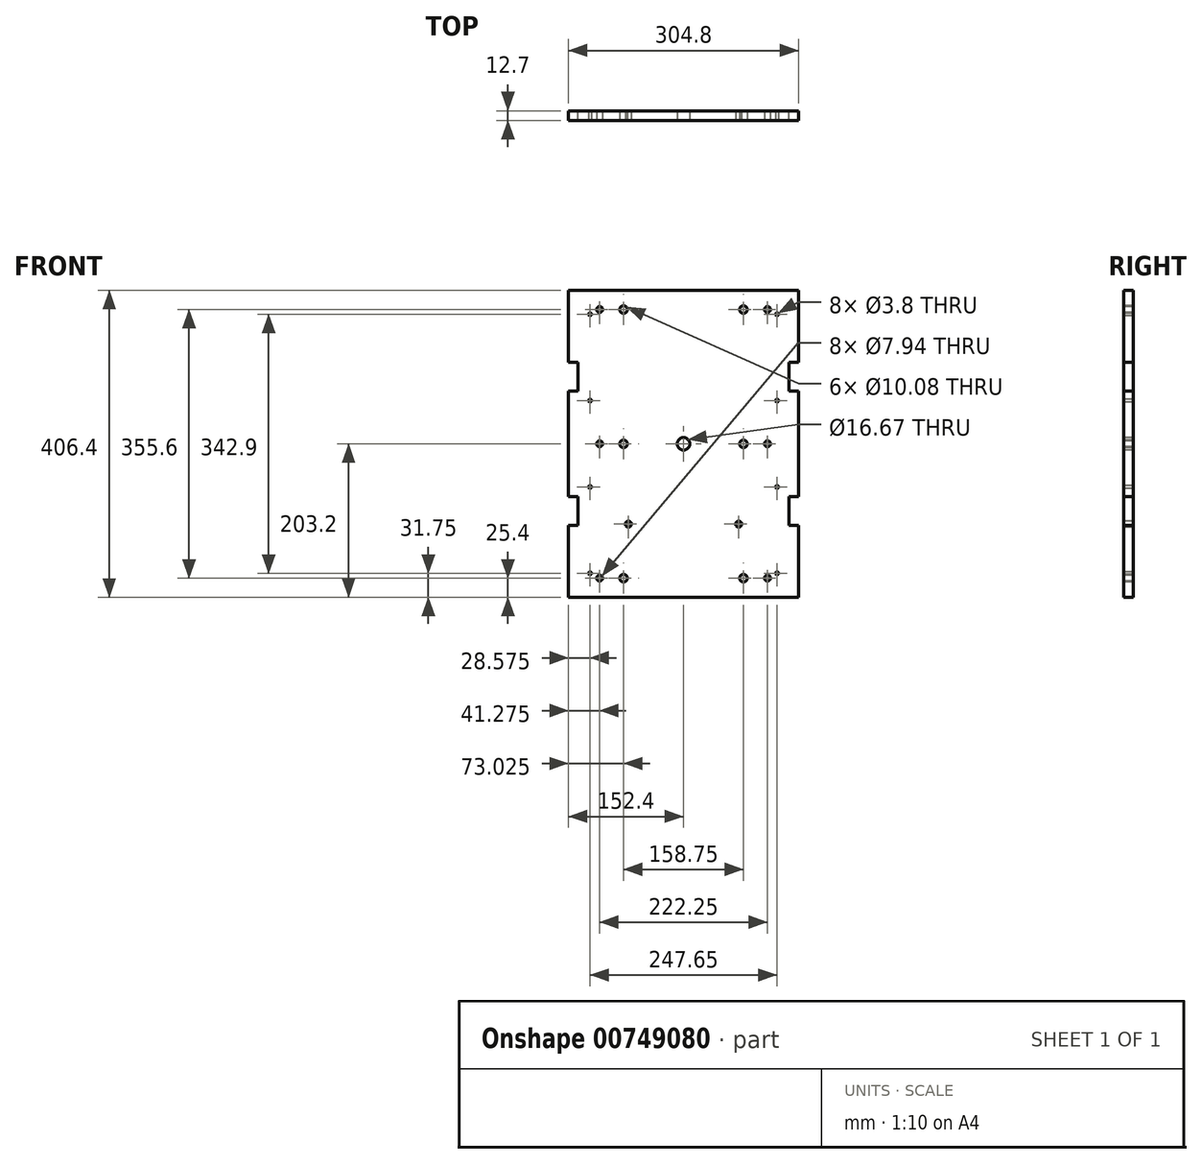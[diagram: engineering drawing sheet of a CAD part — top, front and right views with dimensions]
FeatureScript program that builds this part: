
annotation { "Feature Type Name" : "Feature", "Feature Type Description" : "" }
export const myFeature = defineFeature(function(context is Context, id is Id, definition is map)
    precondition{}
    {
        {
            var Q0;
            Q0=qCreatedBy(makeId("Front.planeOp"),FACE);
            var sketch = newSketch(context, id + "F0", { "sketchPlane" : qUnion([Q0])});
            skLineSegment(sketch, "E0.bottom", {"start": v(0, 0) * mm, "end": v(-304.8, 0) * mm});
            skLineSegment(sketch, "E0.top", {"start": v(0, 406.4) * mm, "end": v(-304.8, 406.4) * mm});
            skLineSegment(sketch, "E0.left", {"start": v(0, 0) * mm, "end": v(0, 95.22) * mm});
            skLineSegment(sketch, "E0.right", {"start": v(-304.8, 0) * mm, "end": v(-304.8, 95.22) * mm});
            skLineSegment(sketch, "E1", {"start": v(-152.4, 0) * mm, "end": v(-152.4, 406.4) * mm, "construction": true});
            skLineSegment(sketch, "E2", {"start": v(-304.8, 203.2) * mm, "end": v(0, 203.2) * mm, "construction": true});
            skPoint(sketch, "E3", {"position": v(-41.28, 381) * mm});
            skPoint(sketch, "E4", {"position": v(-73.03, 381) * mm});
            skLineSegment(sketch, "E5", {"start": v(-73.03, 381) * mm, "end": v(-73.03, 203.2) * mm, "construction": true});
            skLineSegment(sketch, "E6", {"start": v(-41.28, 381) * mm, "end": v(-41.28, 203.2) * mm, "construction": true});
            skPoint(sketch, "E7", {"position": v(-73.03, 203.2) * mm});
            skPoint(sketch, "E8", {"position": v(-41.28, 203.2) * mm});
            skPoint(sketch, "E9", {"position": v(-152.4, 203.2) * mm});
            skLineSegment(sketch, "E10", {"start": v(-28.58, 406.4) * mm, "end": v(-28.58, 203.2) * mm, "construction": true});
            skPoint(sketch, "E11", {"position": v(-28.58, 374.65) * mm});
            skPoint(sketch, "E12", {"position": v(-28.58, 260.35) * mm});
            skPoint(sketch, "E13.MirrorP", {"position": v(-28.58, 146.05) * mm});
            skPoint(sketch, "E14.MirrorP", {"position": v(-28.57, 31.75) * mm});
            skPoint(sketch, "E15.MirrorP", {"position": v(-41.27, 25.4) * mm});
            skPoint(sketch, "E16.MirrorP", {"position": v(-73.02, 25.4) * mm});
            skPoint(sketch, "E17.MirrorP", {"position": v(-276.22, 146.05) * mm});
            skPoint(sketch, "E18.MirrorP", {"position": v(-231.78, 25.4) * mm});
            skPoint(sketch, "E19.MirrorP", {"position": v(-263.53, 25.4) * mm});
            skPoint(sketch, "E20.MirrorP", {"position": v(-276.23, 31.75) * mm});
            skPoint(sketch, "E21.MirrorP", {"position": v(-276.22, 260.35) * mm});
            skPoint(sketch, "E22.MirrorP", {"position": v(-276.23, 374.65) * mm});
            skPoint(sketch, "E23.MirrorP", {"position": v(-263.53, 381) * mm});
            skPoint(sketch, "E24.MirrorP", {"position": v(-231.78, 381) * mm});
            skLineSegment(sketch, "E25", {"start": v(-304.8, 292.1) * mm, "end": v(-152.4, 292.1) * mm, "construction": true});
            skLineSegment(sketch, "E26", {"start": v(-304.8, 311.18) * mm, "end": v(-292.07, 311.18) * mm});
            skLineSegment(sketch, "E27", {"start": v(-292.07, 311.18) * mm, "end": v(-292.07, 273.02) * mm});
            skLineSegment(sketch, "E28", {"start": v(-292.07, 273.02) * mm, "end": v(-304.8, 273.02) * mm});
            skLineSegment(sketch, "E29.trimOffspring", {"start": v(-304.8, 311.18) * mm, "end": v(-304.8, 406.4) * mm});
            skLineSegment(sketch, "E30.MirrorCS", {"start": v(-304.8, 95.22) * mm, "end": v(-292.07, 95.22) * mm});
            skLineSegment(sketch, "E31.MirrorCS", {"start": v(-292.07, 95.22) * mm, "end": v(-292.07, 133.38) * mm});
            skLineSegment(sketch, "E32.MirrorCS", {"start": v(-292.07, 133.38) * mm, "end": v(-304.8, 133.38) * mm});
            skLineSegment(sketch, "E33.MirrorCS", {"start": v(-12.73, 95.22) * mm, "end": v(-12.73, 133.38) * mm});
            skLineSegment(sketch, "E34.MirrorCS", {"start": v(-12.73, 133.38) * mm, "end": v(0, 133.38) * mm});
            skLineSegment(sketch, "E35.MirrorCS", {"start": v(0, 95.22) * mm, "end": v(-12.73, 95.22) * mm});
            skLineSegment(sketch, "E36.MirrorCS", {"start": v(-12.73, 273.02) * mm, "end": v(0, 273.02) * mm});
            skLineSegment(sketch, "E37.MirrorCS", {"start": v(-12.73, 311.18) * mm, "end": v(-12.73, 273.02) * mm});
            skLineSegment(sketch, "E38.MirrorCS", {"start": v(0, 311.18) * mm, "end": v(-12.73, 311.18) * mm});
            skLineSegment(sketch, "E39.trimOffspring", {"start": v(-304.8, 133.38) * mm, "end": v(-304.8, 273.02) * mm});
            skLineSegment(sketch, "E40.trimOffspring", {"start": v(0, 133.38) * mm, "end": v(0, 273.02) * mm});
            skLineSegment(sketch, "E41.trimOffspring", {"start": v(0, 311.18) * mm, "end": v(0, 406.4) * mm});
            skPoint(sketch, "E42.MirrorP", {"position": v(-231.78, 203.2) * mm});
            skPoint(sketch, "E43.MirrorP", {"position": v(-263.53, 203.2) * mm});
            skLineSegment(sketch, "E44", {"start": v(-152.4, 96.84) * mm, "end": v(-304.8, 96.84) * mm, "construction": true});
            skPoint(sketch, "E45", {"position": v(-225.42, 96.84) * mm});
            skPoint(sketch, "E46.MirrorP", {"position": v(-79.38, 96.84) * mm});
            skSolve(sketch);
        }
        {
            var Q0;
            Q0 = qSketchRegion(id + "F0", true);
            extrude(context, id + "F1", {"entities" : qUnion([Q0]), "depth" : 12.7 * mm, "offsetDistance" : 25.4 * mm});
        }
        {
            var Q0;
            Q0=sQuery(id+"F0.wireOp",VERTEX,"E22.MirrorP");
            var Q1;
            Q1=sQuery(id+"F0.wireOp",VERTEX,"E21.MirrorP");
            var Q2;
            Q2=sQuery(id+"F0.wireOp",VERTEX,"E17.MirrorP");
            var Q3;
            Q3=sQuery(id+"F0.wireOp",VERTEX,"E20.MirrorP");
            var Q4;
            Q4=sQuery(id+"F0.wireOp",VERTEX,"E11");
            var Q5;
            Q5=sQuery(id+"F0.wireOp",VERTEX,"E12");
            var Q6;
            Q6=sQuery(id+"F0.wireOp",VERTEX,"E13.MirrorP");
            var Q7;
            Q7=sQuery(id+"F0.wireOp",VERTEX,"E14.MirrorP");
            var Q8;
            Q8=makeQuery(id+"F1.opExtrude","SWEPT_BODY",BODY,{"disambiguationData":[OSD([sQuery(id+"F0.wireOp",EDGE,"E0.bottom"),sQuery(id+"F0.wireOp",EDGE,"E0.top"),sQuery(id+"F0.wireOp",EDGE,"E0.left"),sQuery(id+"F0.wireOp",EDGE,"E0.right"),sQuery(id+"F0.wireOp",EDGE,"E26"),sQuery(id+"F0.wireOp",EDGE,"E27"),sQuery(id+"F0.wireOp",EDGE,"E28"),sQuery(id+"F0.wireOp",EDGE,"E29.trimOffspring"),sQuery(id+"F0.wireOp",EDGE,"E30.MirrorCS"),sQuery(id+"F0.wireOp",EDGE,"E31.MirrorCS"),sQuery(id+"F0.wireOp",EDGE,"E32.MirrorCS"),sQuery(id+"F0.wireOp",EDGE,"E33.MirrorCS"),sQuery(id+"F0.wireOp",EDGE,"E34.MirrorCS"),sQuery(id+"F0.wireOp",EDGE,"E35.MirrorCS"),sQuery(id+"F0.wireOp",EDGE,"E36.MirrorCS"),sQuery(id+"F0.wireOp",EDGE,"E37.MirrorCS"),sQuery(id+"F0.wireOp",EDGE,"E38.MirrorCS"),sQuery(id+"F0.wireOp",EDGE,"E39.trimOffspring"),sQuery(id+"F0.wireOp",EDGE,"E40.trimOffspring"),sQuery(id+"F0.wireOp",EDGE,"E41.trimOffspring")])]});
            hole(context, id + "F2", {"style" : HoleStyle.SIMPLE, "endStyle" : HoleEndStyle.BLIND, "oppositeDirection" : true, "standardTappedOrClearance" : lookupTablePath({ "standard" : "ANSI", "engagement" : "75%", "pitch" : "24 tpi", "size" : "#10", "type" : "Tapped" }), "standardBlindInLast" : lookupTablePath({ "standard" : "ANSI", "engagement" : "75%", "pitch" : "24 tpi", "size" : "#10", "type" : "Tapped" }), "holeDiameter" : 3.8 * mm, "majorDiameter" : 4.83 * mm, "showTappedDepth" : true, "holeDepth" : 15.9 * mm, "isTappedThrough" : true, "tappedDepth" : 12.71 * mm, "tapClearance" : 3, "locations" : qUnion([Q0, Q1, Q2, Q3, Q4, Q5, Q6, Q7]), "scope" : qUnion([Q8])});
        }
        {
            var Q0;
            Q0=sQuery(id+"F0.wireOp",VERTEX,"E9");
            var Q1;
            Q1=makeQuery(id+"F1.opExtrude","SWEPT_BODY",BODY,{"disambiguationData":[OSD([sQuery(id+"F0.wireOp",EDGE,"E0.bottom"),sQuery(id+"F0.wireOp",EDGE,"E0.top"),sQuery(id+"F0.wireOp",EDGE,"E0.left"),sQuery(id+"F0.wireOp",EDGE,"E0.right"),sQuery(id+"F0.wireOp",EDGE,"E26"),sQuery(id+"F0.wireOp",EDGE,"E27"),sQuery(id+"F0.wireOp",EDGE,"E28"),sQuery(id+"F0.wireOp",EDGE,"E29.trimOffspring"),sQuery(id+"F0.wireOp",EDGE,"E30.MirrorCS"),sQuery(id+"F0.wireOp",EDGE,"E31.MirrorCS"),sQuery(id+"F0.wireOp",EDGE,"E32.MirrorCS"),sQuery(id+"F0.wireOp",EDGE,"E33.MirrorCS"),sQuery(id+"F0.wireOp",EDGE,"E34.MirrorCS"),sQuery(id+"F0.wireOp",EDGE,"E35.MirrorCS"),sQuery(id+"F0.wireOp",EDGE,"E36.MirrorCS"),sQuery(id+"F0.wireOp",EDGE,"E37.MirrorCS"),sQuery(id+"F0.wireOp",EDGE,"E38.MirrorCS"),sQuery(id+"F0.wireOp",EDGE,"E39.trimOffspring"),sQuery(id+"F0.wireOp",EDGE,"E40.trimOffspring"),sQuery(id+"F0.wireOp",EDGE,"E41.trimOffspring")])]});
            hole(context, id + "F3", {"style" : HoleStyle.SIMPLE, "endStyle" : HoleEndStyle.BLIND, "oppositeDirection" : true, "standardTappedOrClearance" : lookupTablePath({ "fit" : "Normal (ASME)", "standard" : "ANSI", "size" : "5/8", "type" : "Clearance" }), "standardBlindInLast" : lookupTablePath({ "fit" : "Free", "standard" : "ANSI", "size" : "5/8", "type" : "Clearance" }), "holeDiameter" : 16.67 * mm, "majorDiameter" : 4.83 * mm, "holeDepth" : 15.9 * mm, "isTappedThrough" : true, "tappedDepth" : 12.73 * mm, "tapClearance" : 3, "locations" : qUnion([Q0]), "scope" : qUnion([Q1])});
        }
        {
            var Q0;
            Q0=sQuery(id+"F0.wireOp",VERTEX,"E23.MirrorP");
            var Q1;
            Q1=sQuery(id+"F0.wireOp",VERTEX,"E43.MirrorP");
            var Q2;
            Q2=sQuery(id+"F0.wireOp",VERTEX,"E19.MirrorP");
            var Q3;
            Q3=sQuery(id+"F0.wireOp",VERTEX,"E3");
            var Q4;
            Q4=sQuery(id+"F0.wireOp",VERTEX,"E6.end");
            var Q5;
            Q5=sQuery(id+"F0.wireOp",VERTEX,"E15.MirrorP");
            var Q6;
            Q6=makeQuery(id+"F1.opExtrude","SWEPT_BODY",BODY,{"disambiguationData":[OSD([sQuery(id+"F0.wireOp",EDGE,"E0.bottom"),sQuery(id+"F0.wireOp",EDGE,"E0.top"),sQuery(id+"F0.wireOp",EDGE,"E0.left"),sQuery(id+"F0.wireOp",EDGE,"E0.right"),sQuery(id+"F0.wireOp",EDGE,"E26"),sQuery(id+"F0.wireOp",EDGE,"E27"),sQuery(id+"F0.wireOp",EDGE,"E28"),sQuery(id+"F0.wireOp",EDGE,"E29.trimOffspring"),sQuery(id+"F0.wireOp",EDGE,"E30.MirrorCS"),sQuery(id+"F0.wireOp",EDGE,"E31.MirrorCS"),sQuery(id+"F0.wireOp",EDGE,"E32.MirrorCS"),sQuery(id+"F0.wireOp",EDGE,"E33.MirrorCS"),sQuery(id+"F0.wireOp",EDGE,"E34.MirrorCS"),sQuery(id+"F0.wireOp",EDGE,"E35.MirrorCS"),sQuery(id+"F0.wireOp",EDGE,"E36.MirrorCS"),sQuery(id+"F0.wireOp",EDGE,"E37.MirrorCS"),sQuery(id+"F0.wireOp",EDGE,"E38.MirrorCS"),sQuery(id+"F0.wireOp",EDGE,"E39.trimOffspring"),sQuery(id+"F0.wireOp",EDGE,"E40.trimOffspring"),sQuery(id+"F0.wireOp",EDGE,"E41.trimOffspring")])]});
            hole(context, id + "F4", {"style" : HoleStyle.SIMPLE, "endStyle" : HoleEndStyle.BLIND, "oppositeDirection" : true, "standardTappedOrClearance" : lookupTablePath({ "standard" : "ANSI", "engagement" : "75%", "pitch" : "16 tpi", "size" : "3/8", "type" : "Tapped" }), "standardBlindInLast" : lookupTablePath({ "standard" : "ANSI", "engagement" : "75%", "pitch" : "16 tpi", "size" : "3/8", "type" : "Tapped" }), "holeDiameter" : 7.94 * mm, "majorDiameter" : 9.52 * mm, "showTappedDepth" : true, "holeDepth" : 17.49 * mm, "isTappedThrough" : true, "tappedDepth" : 12.73 * mm, "tapClearance" : 3, "locations" : qUnion([Q0, Q1, Q2, Q3, Q4, Q5]), "scope" : qUnion([Q6])});
        }
        {
            var Q0;
            Q0=sQuery(id+"F0.wireOp",VERTEX,"E24.MirrorP");
            var Q1;
            Q1=sQuery(id+"F0.wireOp",VERTEX,"E42.MirrorP");
            var Q2;
            Q2=sQuery(id+"F0.wireOp",VERTEX,"E18.MirrorP");
            var Q3;
            Q3=sQuery(id+"F0.wireOp",VERTEX,"E16.MirrorP");
            var Q4;
            Q4=sQuery(id+"F0.wireOp",VERTEX,"E7");
            var Q5;
            Q5=sQuery(id+"F0.wireOp",VERTEX,"E5.start");
            var Q6;
            Q6=makeQuery(id+"F1.opExtrude","SWEPT_BODY",BODY,{"disambiguationData":[OSD([sQuery(id+"F0.wireOp",EDGE,"E0.bottom"),sQuery(id+"F0.wireOp",EDGE,"E0.top"),sQuery(id+"F0.wireOp",EDGE,"E0.left"),sQuery(id+"F0.wireOp",EDGE,"E0.right"),sQuery(id+"F0.wireOp",EDGE,"E26"),sQuery(id+"F0.wireOp",EDGE,"E27"),sQuery(id+"F0.wireOp",EDGE,"E28"),sQuery(id+"F0.wireOp",EDGE,"E29.trimOffspring"),sQuery(id+"F0.wireOp",EDGE,"E30.MirrorCS"),sQuery(id+"F0.wireOp",EDGE,"E31.MirrorCS"),sQuery(id+"F0.wireOp",EDGE,"E32.MirrorCS"),sQuery(id+"F0.wireOp",EDGE,"E33.MirrorCS"),sQuery(id+"F0.wireOp",EDGE,"E34.MirrorCS"),sQuery(id+"F0.wireOp",EDGE,"E35.MirrorCS"),sQuery(id+"F0.wireOp",EDGE,"E36.MirrorCS"),sQuery(id+"F0.wireOp",EDGE,"E37.MirrorCS"),sQuery(id+"F0.wireOp",EDGE,"E38.MirrorCS"),sQuery(id+"F0.wireOp",EDGE,"E39.trimOffspring"),sQuery(id+"F0.wireOp",EDGE,"E40.trimOffspring"),sQuery(id+"F0.wireOp",EDGE,"E41.trimOffspring")])]});
            hole(context, id + "F5", {"style" : HoleStyle.SIMPLE, "endStyle" : HoleEndStyle.BLIND, "oppositeDirection" : true, "standardTappedOrClearance" : lookupTablePath({ "fit" : "Normal (ASME)", "standard" : "ANSI", "size" : "3/8", "type" : "Clearance" }), "standardBlindInLast" : lookupTablePath({ "fit" : "Free", "standard" : "ANSI", "size" : "3/8", "type" : "Clearance" }), "holeDiameter" : 10.08 * mm, "majorDiameter" : 9.52 * mm, "holeDepth" : 17.5 * mm, "isTappedThrough" : true, "tappedDepth" : 12.74 * mm, "tapClearance" : 3, "locations" : qUnion([Q0, Q1, Q2, Q3, Q4, Q5]), "scope" : qUnion([Q6])});
        }
        {
            var Q0;
            Q0=sQuery(id+"F0.wireOp",VERTEX,"E45");
            var Q1;
            Q1=sQuery(id+"F0.wireOp",VERTEX,"E46.MirrorP");
            var Q2;
            Q2=makeQuery(id+"F1.opExtrude","SWEPT_BODY",BODY,{"disambiguationData":[OSD([sQuery(id+"F0.wireOp",EDGE,"E0.bottom"),sQuery(id+"F0.wireOp",EDGE,"E0.top"),sQuery(id+"F0.wireOp",EDGE,"E0.left"),sQuery(id+"F0.wireOp",EDGE,"E0.right"),sQuery(id+"F0.wireOp",EDGE,"E26"),sQuery(id+"F0.wireOp",EDGE,"E27"),sQuery(id+"F0.wireOp",EDGE,"E28"),sQuery(id+"F0.wireOp",EDGE,"E29.trimOffspring"),sQuery(id+"F0.wireOp",EDGE,"E30.MirrorCS"),sQuery(id+"F0.wireOp",EDGE,"E31.MirrorCS"),sQuery(id+"F0.wireOp",EDGE,"E32.MirrorCS"),sQuery(id+"F0.wireOp",EDGE,"E33.MirrorCS"),sQuery(id+"F0.wireOp",EDGE,"E34.MirrorCS"),sQuery(id+"F0.wireOp",EDGE,"E35.MirrorCS"),sQuery(id+"F0.wireOp",EDGE,"E36.MirrorCS"),sQuery(id+"F0.wireOp",EDGE,"E37.MirrorCS"),sQuery(id+"F0.wireOp",EDGE,"E38.MirrorCS"),sQuery(id+"F0.wireOp",EDGE,"E39.trimOffspring"),sQuery(id+"F0.wireOp",EDGE,"E40.trimOffspring"),sQuery(id+"F0.wireOp",EDGE,"E41.trimOffspring")])]});
            hole(context, id + "F6", {"style" : HoleStyle.SIMPLE, "endStyle" : HoleEndStyle.BLIND, "oppositeDirection" : true, "standardTappedOrClearance" : lookupTablePath({ "standard" : "ANSI", "engagement" : "75%", "pitch" : "16 tpi", "size" : "3/8", "type" : "Tapped" }), "standardBlindInLast" : lookupTablePath({ "standard" : "ANSI", "engagement" : "75%", "pitch" : "16 tpi", "size" : "3/8", "type" : "Tapped" }), "holeDiameter" : 7.94 * mm, "majorDiameter" : 9.52 * mm, "showTappedDepth" : true, "holeDepth" : 20.68 * mm, "isTappedThrough" : true, "tappedDepth" : 15.9 * mm, "tapClearance" : 3, "locations" : qUnion([Q0, Q1]), "scope" : qUnion([Q2])});
        }
    });
